FCSTD DOCUMENT  (FreeCAD 0.19R24276 (Git))
Label: Temp_H_floor
License: All rights reserved
LicenseURL: http://en.wikipedia.org/wiki/All_rights_reserved
objects: Sketcher::SketchObject×1, PartDesign::Body×1
note: 2 computed .brp shape members not serialized (recipe doc carries the construction recipe); baked Part::Feature solids carry a one-line shape summary decoded from their .brp

FEATURE [Sketcher::SketchObject] Sketch
  FullyConstrained = false
  MapMode = 5
  Support = -> [XY_Plane]
  sketch-geometry (16):
    g0: LineSegment StartX=0 StartY=0 StartZ=0 EndX=7.19274 EndY=0 EndZ=0
    g1: LineSegment StartX=7.19274 StartY=0 StartZ=0 EndX=7.19274 EndY=30 EndZ=0
    g2: LineSegment StartX=7.19274 StartY=30 StartZ=0 EndX=0 EndY=30 EndZ=0
    g3: LineSegment StartX=0 StartY=30 StartZ=0 EndX=0 EndY=0 EndZ=0
    g4: LineSegment StartX=17.2486 StartY=10.9337 StartZ=0 EndX=29.5391 EndY=10.9337 EndZ=0
    g5: LineSegment StartX=29.5391 StartY=10.9337 StartZ=0 EndX=29.5391 EndY=5.93368 EndZ=0
    g6: LineSegment StartX=29.5391 StartY=5.93368 StartZ=0 EndX=17.2486 EndY=5.93368 EndZ=0
    g7: LineSegment StartX=17.2486 StartY=5.93368 StartZ=0 EndX=17.2486 EndY=10.9337 EndZ=0
    g8: LineSegment StartX=17.2486 StartY=21.9337 StartZ=0 EndX=29.5391 EndY=21.9337 EndZ=0
    g9: LineSegment StartX=29.5391 StartY=21.9337 StartZ=0 EndX=29.5391 EndY=16.9337 EndZ=0
    g10: LineSegment StartX=29.5391 StartY=16.9337 StartZ=0 EndX=17.2486 EndY=16.9337 EndZ=0
    g11: LineSegment StartX=17.2486 StartY=16.9337 StartZ=0 EndX=17.2486 EndY=21.9337 EndZ=0
    g12: LineSegment StartX=17.2486 StartY=16.9337 StartZ=0 EndX=25.0698 EndY=16.9337 EndZ=0
    g13: LineSegment StartX=25.0698 StartY=16.9337 StartZ=0 EndX=25.0698 EndY=10.9337 EndZ=0
    g14: LineSegment StartX=25.0698 StartY=10.9337 StartZ=0 EndX=17.2486 EndY=10.9337 EndZ=0
    g15: LineSegment StartX=17.2486 StartY=10.9337 StartZ=0 EndX=17.2486 EndY=16.9337 EndZ=0
  constraints (39):
    c: Coincident(g0,g1)
    c: Coincident(g1,g2)
    c: Coincident(g2,g3)
    c: Coincident(g3,g0)
    c: Horizontal(g0)
    c: Horizontal(g2)
    c: Vertical(g1)
    c: Vertical(g3)
    c: Coincident(g0,g-1)
    c: DistanceY(g3,g3) = 30
    c: Coincident(g4,g5)
    c: Coincident(g5,g6)
    c: Coincident(g6,g7)
    c: Coincident(g7,g4)
    c: Horizontal(g4)
    c: Horizontal(g6)
    c: Vertical(g5)
    c: Vertical(g7)
    c: Coincident(g8,g9)
    c: Coincident(g9,g10)
    c: Coincident(g10,g11)
    c: Coincident(g11,g8)
    c: Horizontal(g8)
    c: Horizontal(g10)
    c: Vertical(g9)
    c: Vertical(g11)
    c: Coincident(g12,g13)
    c: Coincident(g13,g14)
    c: Coincident(g14,g15)
    c: Coincident(g15,g12)
    c: Horizontal(g12)
    c: Horizontal(g14)
    c: Vertical(g13)
    c: Vertical(g15)
    c: DistanceY(g13,g13) = 6
    c: DistanceY(g5,g5) = 5
    c: DistanceY(g9,g9) = 5
    c: Coincident(g10,g12)
    c: Coincident(g4,g14)
FEATURE [PartDesign::Body] Body
  Group = -> [Sketch]
  Origin = -> Origin
